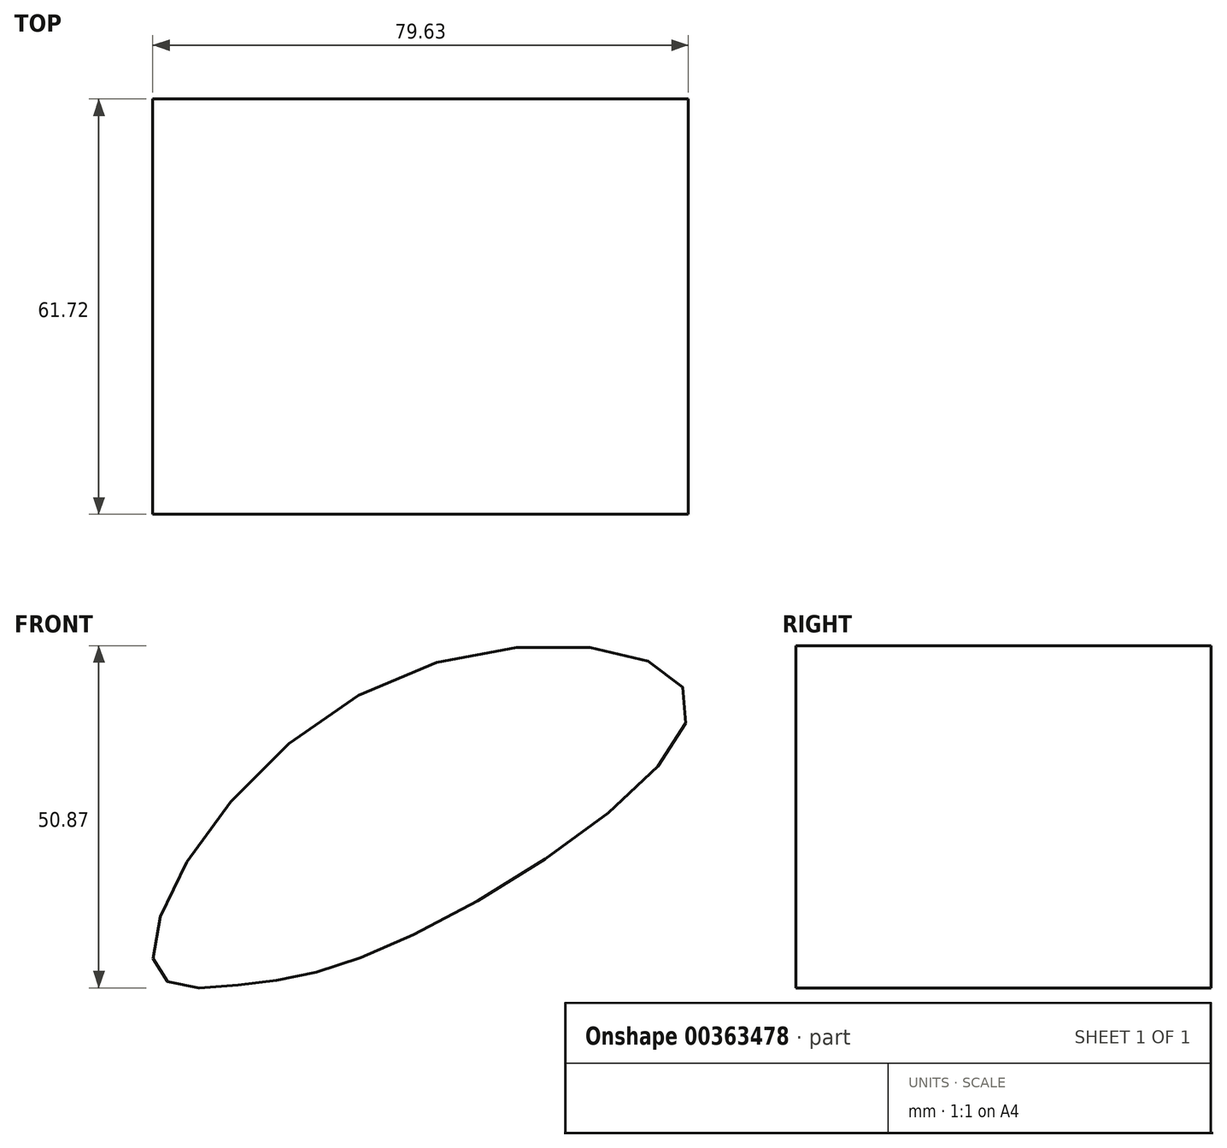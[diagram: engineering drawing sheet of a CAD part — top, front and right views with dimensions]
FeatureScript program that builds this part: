
annotation { "Feature Type Name" : "Feature", "Feature Type Description" : "" }
export const myFeature = defineFeature(function(context is Context, id is Id, definition is map)
    precondition{}
    {
        {
            var Q0;
            Q0=qCreatedBy(makeId("Front.planeOp"),FACE);
            var sketch = newSketch(context, id + "F0", { "sketchPlane" : qUnion([Q0])});
            skFitSpline(sketch, "E0", {"points": [v(25.87, 7.47) * mm, v(66.63, 42.16) * mm, v(20.38, 44.49) * mm, v(-12.54, 2.45) * mm, v(0, 0) * mm, v(25.87, 7.47) * mm]});
            skSolve(sketch);
        }
        {
            var Q0;
            Q0=makeQuery(id+"F0.imprint","IMPRINT",FACE,{"disambiguationData":[TD([[makeQuery(id+"F0.imprint","IMPRINT",EDGE,{"derivedFrom":sQuery(id+"F0.wireOp",EDGE,"E0")}),1.0]])]});
            extrude(context, id + "F1", {"entities" : qUnion([Q0]), "depth" : 61.72 * mm});
        }
    });
